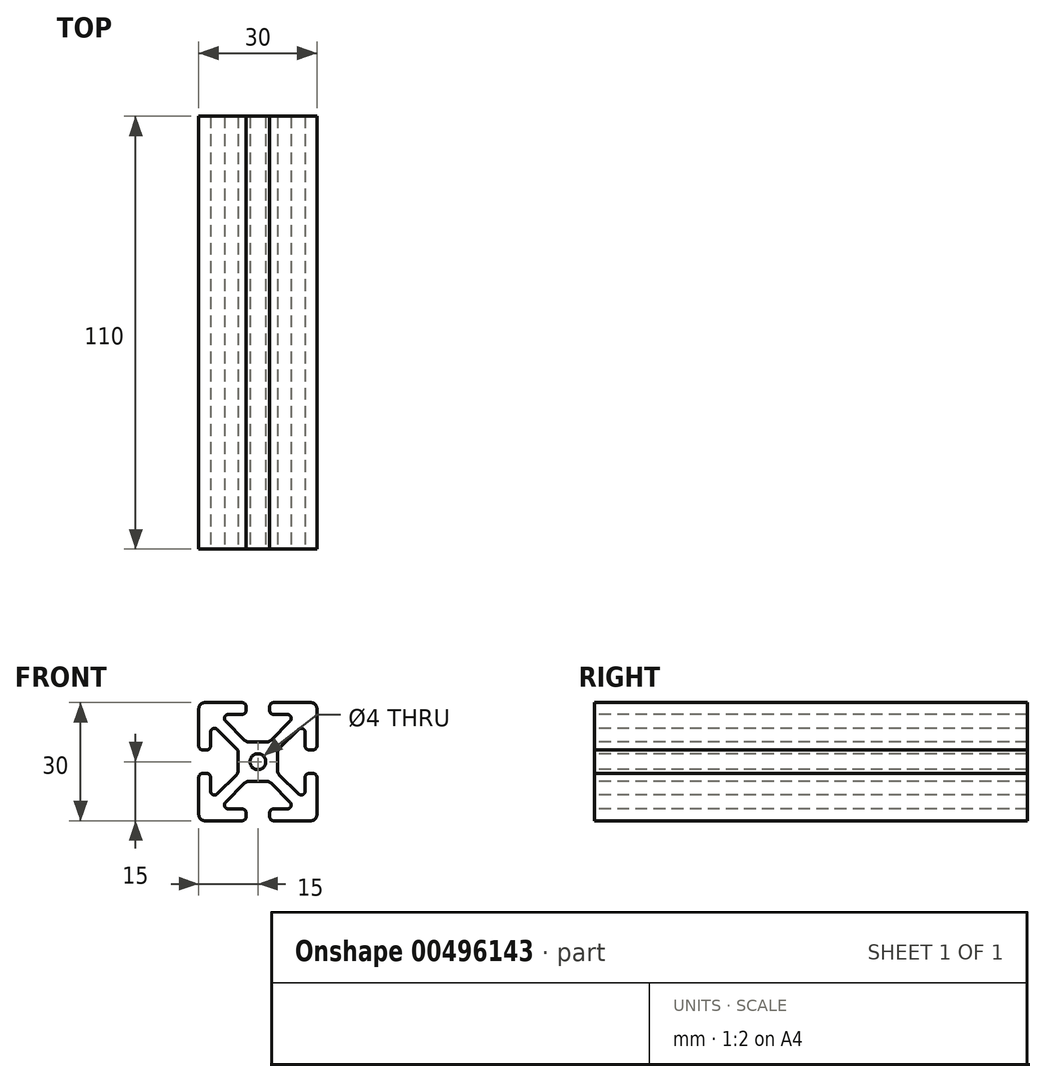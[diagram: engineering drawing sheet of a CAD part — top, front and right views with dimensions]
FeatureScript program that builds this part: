
annotation { "Feature Type Name" : "Feature", "Feature Type Description" : "" }
export const myFeature = defineFeature(function(context is Context, id is Id, definition is map)
    precondition{}
    {
        {
            var Q0;
            Q0=qCreatedBy(makeId("Front.planeOp"),FACE);
            var sketch = newSketch(context, id + "F0", { "sketchPlane" : qUnion([Q0])});
            skLineSegment(sketch, "E0.bottom", {"start": v(13.5, 15) * mm, "end": v(4, 15) * mm});
            skLineSegment(sketch, "E0.top", {"start": v(13.5, -15) * mm, "end": v(4, -15) * mm});
            skLineSegment(sketch, "E0.left", {"start": v(15, 13.5) * mm, "end": v(15, 4) * mm});
            skLineSegment(sketch, "E0.right", {"start": v(-15, 13.5) * mm, "end": v(-15, 4) * mm});
            skPoint(sketch, "E0.middle", {"position": v(0, 0) * mm});
            skLineSegment(sketch, "E1.bottom", {"start": v(7.46, 12) * mm, "end": v(4, 12) * mm});
            skLineSegment(sketch, "E1.top", {"start": v(7.46, -12) * mm, "end": v(4, -12) * mm});
            skLineSegment(sketch, "E1.left", {"start": v(12, 7.46) * mm, "end": v(12, 4) * mm});
            skLineSegment(sketch, "E1.right", {"start": v(-12, 7.46) * mm, "end": v(-12, 4) * mm});
            skLineSegment(sketch, "E2", {"start": v(8.17, 10.3) * mm, "end": v(3.32, 5.44) * mm});
            skLineSegment(sketch, "E3", {"start": v(-8.17, -10.3) * mm, "end": v(-3.32, -5.44) * mm});
            skLineSegment(sketch, "E4", {"start": v(-8.17, 10.3) * mm, "end": v(-3.32, 5.44) * mm});
            skLineSegment(sketch, "E5", {"start": v(-10.3, 8.17) * mm, "end": v(-5, 2.88) * mm});
            skPoint(sketch, "E6.orphan", {"position": v(12, 12) * mm});
            skPoint(sketch, "E7.orphan", {"position": v(12, -12) * mm});
            skPoint(sketch, "E8.orphan", {"position": v(-12, -12) * mm});
            skPoint(sketch, "E9.orphan", {"position": v(-12, 12) * mm});
            skLineSegment(sketch, "E10.trimOffspring", {"start": v(-5.44, -3.32) * mm, "end": v(-10.3, -8.17) * mm});
            skLineSegment(sketch, "E11.trimOffspring", {"start": v(5.44, -3.32) * mm, "end": v(10.3, -8.17) * mm});
            skLineSegment(sketch, "E12.trimOffspring", {"start": v(5.44, 3.32) * mm, "end": v(10.3, 8.17) * mm});
            skLineSegment(sketch, "E13.trimOffspring", {"start": v(3.32, -5.44) * mm, "end": v(8.17, -10.3) * mm});
            skLineSegment(sketch, "E14.bottom", {"start": v(2.26, 5) * mm, "end": v(-2.26, 5) * mm});
            skLineSegment(sketch, "E14.top", {"start": v(2.26, -5) * mm, "end": v(-2.26, -5) * mm});
            skLineSegment(sketch, "E14.left", {"start": v(5, 2.26) * mm, "end": v(5, -2.26) * mm});
            skLineSegment(sketch, "E14.right", {"start": v(-5, 2.88) * mm, "end": v(-5, -2.26) * mm});
            skPoint(sketch, "E15.orphan", {"position": v(5, 5) * mm});
            skPoint(sketch, "E16.orphan", {"position": v(5, -5) * mm});
            skPoint(sketch, "E17.orphan", {"position": v(-5, -5) * mm});
            skPoint(sketch, "E18.orphan", {"position": v(-5, 5) * mm});
            skCircle(sketch, "E19", {"center": v(0, 0) * mm, "radius": 2 * mm});
            skLineSegment(sketch, "E20", {"start": v(-3, 14) * mm, "end": v(-3, 13) * mm});
            skLineSegment(sketch, "E21", {"start": v(3, 14) * mm, "end": v(3, 13) * mm});
            skLineSegment(sketch, "E22.trimOffspring", {"start": v(-3, -13) * mm, "end": v(-3, -14) * mm});
            skLineSegment(sketch, "E23.trimOffspring", {"start": v(-4, 12) * mm, "end": v(-7.46, 12) * mm});
            skLineSegment(sketch, "E24.trimOffspring", {"start": v(-4, 15) * mm, "end": v(-13.5, 15) * mm});
            skLineSegment(sketch, "E25.trimOffspring", {"start": v(3, -13) * mm, "end": v(3, -14) * mm});
            skLineSegment(sketch, "E26.trimOffspring", {"start": v(-4, -12) * mm, "end": v(-7.46, -12) * mm});
            skLineSegment(sketch, "E27.trimOffspring", {"start": v(-4, -15) * mm, "end": v(-13.5, -15) * mm});
            skLineSegment(sketch, "E28", {"start": v(-14, 3) * mm, "end": v(-13, 3) * mm});
            skLineSegment(sketch, "E29", {"start": v(-14, -3) * mm, "end": v(-13, -3) * mm});
            skLineSegment(sketch, "E30.trimOffspring", {"start": v(-12, -4) * mm, "end": v(-12, -7.46) * mm});
            skLineSegment(sketch, "E31.trimOffspring", {"start": v(-15, -4) * mm, "end": v(-15, -13.5) * mm});
            skLineSegment(sketch, "E32.trimOffspring", {"start": v(13, 3) * mm, "end": v(14, 3) * mm});
            skLineSegment(sketch, "E33.trimOffspring", {"start": v(13, -3) * mm, "end": v(14, -3) * mm});
            skLineSegment(sketch, "E34.trimOffspring", {"start": v(12, -4) * mm, "end": v(12, -7.46) * mm});
            skLineSegment(sketch, "E35.trimOffspring", {"start": v(15, -4) * mm, "end": v(15, -13.5) * mm});
            skPoint(sketch, "E36.visualSharp", {"position": v(-15, 15) * mm});
            skArc(sketch, "E36.filletArc", {"start": v(-13.5, 15) * mm, "mid": v(-14.56, 14.56) * mm, "end": v(-15, 13.5) * mm});
            skPoint(sketch, "E37.visualSharp", {"position": v(15, 15) * mm});
            skArc(sketch, "E37.filletArc", {"start": v(15, 13.5) * mm, "mid": v(14.56, 14.56) * mm, "end": v(13.5, 15) * mm});
            skPoint(sketch, "E38.visualSharp", {"position": v(15, -15) * mm});
            skArc(sketch, "E38.filletArc", {"start": v(13.5, -15) * mm, "mid": v(14.56, -14.56) * mm, "end": v(15, -13.5) * mm});
            skPoint(sketch, "E39.visualSharp", {"position": v(-15, -15) * mm});
            skArc(sketch, "E39.filletArc", {"start": v(-15, -13.5) * mm, "mid": v(-14.56, -14.56) * mm, "end": v(-13.5, -15) * mm});
            skPoint(sketch, "E40.visualSharp", {"position": v(-5, -2.88) * mm});
            skArc(sketch, "E40.filletArc", {"start": v(-5.44, -3.32) * mm, "mid": v(-5.11, -2.83) * mm, "end": v(-5, -2.26) * mm});
            skPoint(sketch, "E41.visualSharp", {"position": v(-2.88, -5) * mm});
            skArc(sketch, "E41.filletArc", {"start": v(-2.26, -5) * mm, "mid": v(-2.83, -5.11) * mm, "end": v(-3.32, -5.44) * mm});
            skPoint(sketch, "E42.visualSharp", {"position": v(2.88, -5) * mm});
            skArc(sketch, "E42.filletArc", {"start": v(3.32, -5.44) * mm, "mid": v(2.83, -5.11) * mm, "end": v(2.26, -5) * mm});
            skPoint(sketch, "E43.visualSharp", {"position": v(5, -2.88) * mm});
            skArc(sketch, "E43.filletArc", {"start": v(5, -2.26) * mm, "mid": v(5.11, -2.83) * mm, "end": v(5.44, -3.32) * mm});
            skPoint(sketch, "E44.visualSharp", {"position": v(5, 2.88) * mm});
            skArc(sketch, "E44.filletArc", {"start": v(5.44, 3.32) * mm, "mid": v(5.11, 2.83) * mm, "end": v(5, 2.26) * mm});
            skPoint(sketch, "E45.visualSharp", {"position": v(2.88, 5) * mm});
            skArc(sketch, "E45.filletArc", {"start": v(2.26, 5) * mm, "mid": v(2.83, 5.11) * mm, "end": v(3.32, 5.44) * mm});
            skPoint(sketch, "E46.visualSharp", {"position": v(-2.88, 5) * mm});
            skArc(sketch, "E46.filletArc", {"start": v(-3.32, 5.44) * mm, "mid": v(-2.83, 5.11) * mm, "end": v(-2.26, 5) * mm});
            skPoint(sketch, "E47.visualSharp", {"position": v(-3, 12) * mm});
            skArc(sketch, "E47.filletArc", {"start": v(-4, 12) * mm, "mid": v(-3.3, 12.3) * mm, "end": v(-3, 13) * mm});
            skPoint(sketch, "E48.visualSharp", {"position": v(-3, 15) * mm});
            skArc(sketch, "E48.filletArc", {"start": v(-3, 14) * mm, "mid": v(-3.3, 14.7) * mm, "end": v(-4, 15) * mm});
            skPoint(sketch, "E49.visualSharp", {"position": v(3, 15) * mm});
            skArc(sketch, "E49.filletArc", {"start": v(4, 15) * mm, "mid": v(3.3, 14.7) * mm, "end": v(3, 14) * mm});
            skPoint(sketch, "E50.visualSharp", {"position": v(3, 12) * mm});
            skArc(sketch, "E50.filletArc", {"start": v(3, 13) * mm, "mid": v(3.3, 12.3) * mm, "end": v(4, 12) * mm});
            skPoint(sketch, "E51.visualSharp", {"position": v(12, 3) * mm});
            skArc(sketch, "E51.filletArc", {"start": v(12, 4) * mm, "mid": v(12.3, 3.3) * mm, "end": v(13, 3) * mm});
            skPoint(sketch, "E52.visualSharp", {"position": v(15, 3) * mm});
            skArc(sketch, "E52.filletArc", {"start": v(14, 3) * mm, "mid": v(14.7, 3.3) * mm, "end": v(15, 4) * mm});
            skPoint(sketch, "E53.visualSharp", {"position": v(15, -3) * mm});
            skArc(sketch, "E53.filletArc", {"start": v(15, -4) * mm, "mid": v(14.7, -3.3) * mm, "end": v(14, -3) * mm});
            skPoint(sketch, "E54.visualSharp", {"position": v(12, -3) * mm});
            skArc(sketch, "E54.filletArc", {"start": v(13, -3) * mm, "mid": v(12.3, -3.3) * mm, "end": v(12, -4) * mm});
            skPoint(sketch, "E55.visualSharp", {"position": v(3, -12) * mm});
            skArc(sketch, "E55.filletArc", {"start": v(4, -12) * mm, "mid": v(3.3, -12.3) * mm, "end": v(3, -13) * mm});
            skPoint(sketch, "E56.visualSharp", {"position": v(3, -15) * mm});
            skArc(sketch, "E56.filletArc", {"start": v(3, -14) * mm, "mid": v(3.3, -14.7) * mm, "end": v(4, -15) * mm});
            skPoint(sketch, "E57.visualSharp", {"position": v(-3, -12) * mm});
            skArc(sketch, "E57.filletArc", {"start": v(-3, -13) * mm, "mid": v(-3.3, -12.3) * mm, "end": v(-4, -12) * mm});
            skPoint(sketch, "E58.visualSharp", {"position": v(-3, -15) * mm});
            skArc(sketch, "E58.filletArc", {"start": v(-4, -15) * mm, "mid": v(-3.3, -14.7) * mm, "end": v(-3, -14) * mm});
            skPoint(sketch, "E59.visualSharp", {"position": v(-12, -3) * mm});
            skArc(sketch, "E59.filletArc", {"start": v(-12, -4) * mm, "mid": v(-12.3, -3.3) * mm, "end": v(-13, -3) * mm});
            skPoint(sketch, "E60.visualSharp", {"position": v(-15, -3) * mm});
            skArc(sketch, "E60.filletArc", {"start": v(-14, -3) * mm, "mid": v(-14.7, -3.3) * mm, "end": v(-15, -4) * mm});
            skPoint(sketch, "E61.visualSharp", {"position": v(-15, 3) * mm});
            skArc(sketch, "E61.filletArc", {"start": v(-15, 4) * mm, "mid": v(-14.7, 3.3) * mm, "end": v(-14, 3) * mm});
            skPoint(sketch, "E62.visualSharp", {"position": v(-12, 3) * mm});
            skArc(sketch, "E62.filletArc", {"start": v(-13, 3) * mm, "mid": v(-12.3, 3.3) * mm, "end": v(-12, 4) * mm});
            skPoint(sketch, "E63.visualSharp", {"position": v(9.88, 12) * mm});
            skArc(sketch, "E63.filletArc", {"start": v(8.17, 10.3) * mm, "mid": v(8.39, 11.38) * mm, "end": v(7.46, 12) * mm});
            skPoint(sketch, "E64.visualSharp", {"position": v(12, 9.88) * mm});
            skArc(sketch, "E64.filletArc", {"start": v(12, 7.46) * mm, "mid": v(11.38, 8.39) * mm, "end": v(10.3, 8.17) * mm});
            skPoint(sketch, "E65.visualSharp", {"position": v(12, -9.88) * mm});
            skArc(sketch, "E65.filletArc", {"start": v(10.3, -8.17) * mm, "mid": v(11.38, -8.39) * mm, "end": v(12, -7.46) * mm});
            skPoint(sketch, "E66.visualSharp", {"position": v(9.88, -12) * mm});
            skArc(sketch, "E66.filletArc", {"start": v(7.46, -12) * mm, "mid": v(8.39, -11.38) * mm, "end": v(8.17, -10.3) * mm});
            skPoint(sketch, "E67.visualSharp", {"position": v(-12, -9.88) * mm});
            skArc(sketch, "E67.filletArc", {"start": v(-12, -7.46) * mm, "mid": v(-11.38, -8.39) * mm, "end": v(-10.3, -8.17) * mm});
            skPoint(sketch, "E68.visualSharp", {"position": v(-9.88, -12) * mm});
            skArc(sketch, "E68.filletArc", {"start": v(-8.17, -10.3) * mm, "mid": v(-8.39, -11.38) * mm, "end": v(-7.46, -12) * mm});
            skPoint(sketch, "E69.visualSharp", {"position": v(-12, 9.88) * mm});
            skArc(sketch, "E69.filletArc", {"start": v(-10.3, 8.17) * mm, "mid": v(-11.38, 8.39) * mm, "end": v(-12, 7.46) * mm});
            skPoint(sketch, "E70.visualSharp", {"position": v(-9.88, 12) * mm});
            skArc(sketch, "E70.filletArc", {"start": v(-7.46, 12) * mm, "mid": v(-8.39, 11.38) * mm, "end": v(-8.17, 10.3) * mm});
            skSolve(sketch);
        }
        {
            var Q0;
            Q0=qSketchRegion(id+"F0",true);
            extrude(context, id + "F1", {"entities" : qUnion([Q0]), "oppositeDirection" : true, "depth" : 110 * mm});
        }
    });
